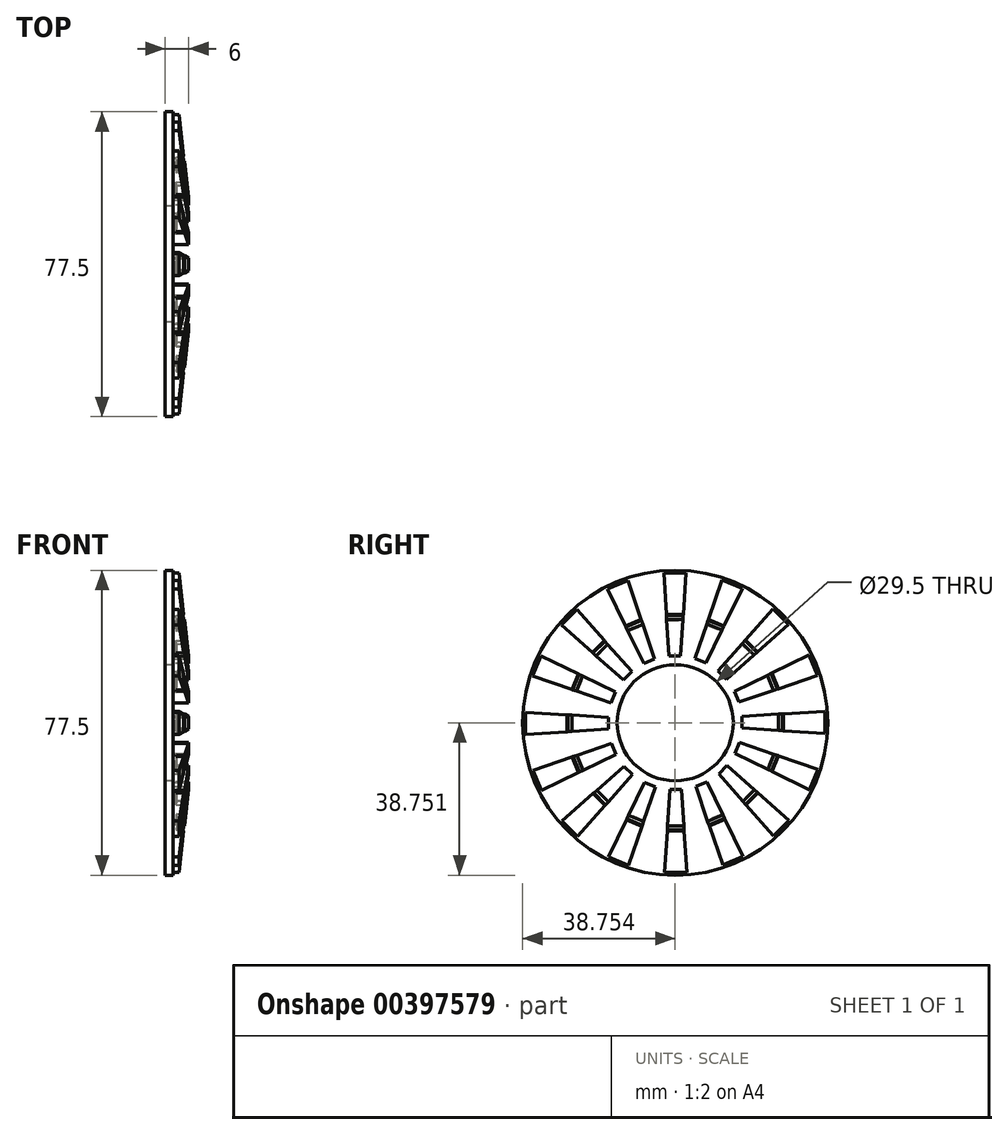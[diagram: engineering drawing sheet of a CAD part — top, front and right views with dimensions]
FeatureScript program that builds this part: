
annotation { "Feature Type Name" : "Feature", "Feature Type Description" : "" }
export const myFeature = defineFeature(function(context is Context, id is Id, definition is map)
    precondition{}
    {
        {
            var Q0;
            Q0=qCreatedBy(makeId("Front.planeOp"),FACE);
            var sketch = newSketch(context, id + "F0", { "sketchPlane" : qUnion([Q0])});
            skLineSegment(sketch, "E0", {"start": v(0, 0) * mm, "end": v(0, 21) * mm});
            skLineSegment(sketch, "E1", {"start": v(0, 21) * mm, "end": v(3.5, 21) * mm});
            skLineSegment(sketch, "E2", {"start": v(3.5, 21) * mm, "end": v(6, 0) * mm});
            skLineSegment(sketch, "E3", {"start": v(6, 0) * mm, "end": v(0, 0) * mm});
            skSolve(sketch);
        }
        {
            var Q0;
            Q0=qSketchRegion(id+"F0",true);
            extrude(context, id + "F1", {"entities" : qUnion([Q0]), "depth" : 6 * mm});
        }
        {
            var Q0;
            Q0=makeQuery(id+"F1.opExtrude","SWEPT_FACE",FACE,{"disambiguationData":[OSD([sQuery(id+"F0.wireOp",EDGE,"E2")])]});
            var sketch = newSketch(context, id + "F2", { "sketchPlane" : qUnion([Q0])});
            skLineSegment(sketch, "E4.bottom", {"start": v(-6, 9.86) * mm, "end": v(0, 9.86) * mm});
            skLineSegment(sketch, "E4.top", {"start": v(-6, 8.61) * mm, "end": v(0, 8.61) * mm});
            skLineSegment(sketch, "E4.left", {"start": v(-6, 9.86) * mm, "end": v(-6, 8.61) * mm});
            skLineSegment(sketch, "E4.right", {"start": v(0, 9.86) * mm, "end": v(0, 8.61) * mm});
            skSolve(sketch);
        }
        {
            var Q0;
            Q0=makeQuery(id+"F2.imprint","IMPRINT",FACE,{"disambiguationData":[TD([[makeQuery(id+"F2.imprint","IMPRINT",EDGE,{"derivedFrom":sQuery(id+"F2.wireOp",EDGE,"E4.bottom")}),-1.0]])]});
            extrude(context, id + "F3", {"entities" : qUnion([Q0]), "operationType" : NewBodyOperationType.REMOVE, "oppositeDirection" : true, "depth" : 2 * mm});
        }
        {
            var Q0;
            Q0=makeQuery(id+"F1.opExtrude","CAP_EDGE",EDGE,{"disambiguationData":[OSD([sQuery(id+"F0.wireOp",EDGE,"E3")])],"isStart":false});
            var Q1;
            Q1=makeQuery(id+"F1.opExtrude","CAP_EDGE",EDGE,{"disambiguationData":[OSD([sQuery(id+"F0.wireOp",EDGE,"E3")])],"isStart":true});
            chamfer(context, id + "F4", {"entities" : qUnion([Q0, Q1]), "chamferType" : ChamferType.TWO_OFFSETS, "width1" : 1.5 * mm, "oppositeDirection" : false, "width2" : 24.25 * mm, "tangentPropagation" : true});
        }
        {
            var Q0;
            Q0=qCreatedBy(makeId("Right.planeOp"),FACE);
            var sketch = newSketch(context, id + "F5", { "sketchPlane" : qUnion([Q0])});
            skLineSegment(sketch, "E5", {"start": v(-3, 0) * mm, "end": v(-2.88, -17) * mm});
            skCircle(sketch, "E6", {"center": v(-2.88, -17) * mm, "radius": 14.75 * mm});
            skCircle(sketch, "E7", {"center": v(-2.88, -17) * mm, "radius": 38.75 * mm});
            skSolve(sketch);
        }
        {
            var Q0;
            Q0=makeQuery(id+"F1.opExtrude","SWEPT_BODY",BODY,{"disambiguationData":[OSD([sQuery(id+"F0.wireOp",EDGE,"E0"),sQuery(id+"F0.wireOp",EDGE,"E1"),sQuery(id+"F0.wireOp",EDGE,"E2"),sQuery(id+"F0.wireOp",EDGE,"E3")])]});
            var Q1;
            Q1=sQuery(id+"F5.wireOp",EDGE,"E7");
            circularPattern(context, id + "F6", {"entities" : qUnion([Q0]), "axis" : qUnion([Q1]), "angle" : 360 * degree, "instanceCount" : 16, "equalSpace" : true});
        }
        {
            var Q0;
            Q0=qSketchRegion(id+"F5",true);
            extrude(context, id + "F7", {"entities" : qUnion([Q0]), "operationType" : NewBodyOperationType.ADD, "depth" : 2 * mm});
        }
    });
